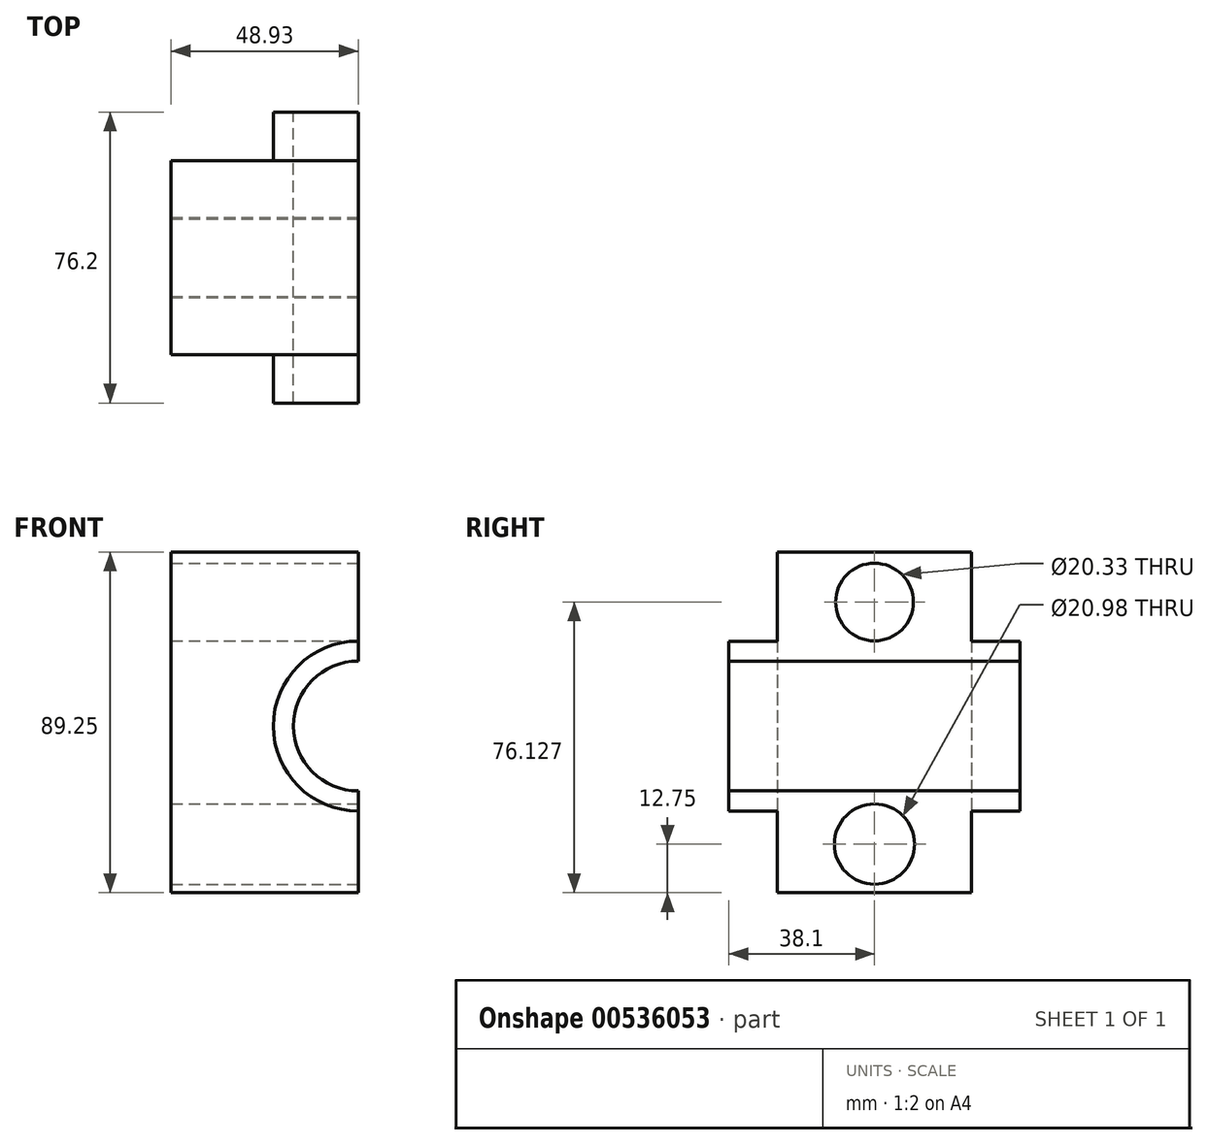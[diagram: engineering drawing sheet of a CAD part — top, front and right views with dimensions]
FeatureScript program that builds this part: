
annotation { "Feature Type Name" : "Feature", "Feature Type Description" : "" }
export const myFeature = defineFeature(function(context is Context, id is Id, definition is map)
    precondition{}
    {
        {
            var Q0;
            Q0=qCreatedBy(makeId("Front.planeOp"),FACE);
            var sketch = newSketch(context, id + "F0", { "sketchPlane" : qUnion([Q0])});
            skLineSegment(sketch, "E0.bottom", {"start": v(-48.93, 45.58) * mm, "end": v(47.02, 45.58) * mm});
            skLineSegment(sketch, "E0.top", {"start": v(-48.93, -43.67) * mm, "end": v(47.02, -43.67) * mm});
            skLineSegment(sketch, "E0.left", {"start": v(-48.93, 45.58) * mm, "end": v(-48.93, -43.67) * mm});
            skLineSegment(sketch, "E0.right", {"start": v(47.02, 45.58) * mm, "end": v(47.02, -43.67) * mm});
            skCircle(sketch, "E1", {"center": v(0, 0) * mm, "radius": 22.22 * mm});
            skCircle(sketch, "E2", {"center": v(0, 0) * mm, "radius": 16.98 * mm});
            skSolve(sketch);
        }
        {
            var Q0;
            Q0 = qSketchRegion(id + "F0", true);
            extrude(context, id + "F1", {"entities" : qUnion([Q0]), "endBound" : BoundingType.SYMMETRIC, "depth" : 50.8 * mm, "offsetDistance" : 25.4 * mm});
        }
        {
            var Q0;
            Q0=makeQuery(id+"F0.imprint","IMPRINT",FACE,{"disambiguationData":[TD([[makeQuery(id+"F0.imprint","IMPRINT",EDGE,{"derivedFrom":sQuery(id+"F0.wireOp",EDGE,"E1")}),1.0]])]});
            extrude(context, id + "F2", {"entities" : qUnion([Q0]), "operationType" : NewBodyOperationType.ADD, "endBound" : BoundingType.SYMMETRIC, "depth" : 76.2 * mm, "offsetDistance" : 25.4 * mm});
        }
        {
            var Q0;
            Q0=qCreatedBy(makeId("Top.planeOp"),FACE);
            var sketch = newSketch(context, id + "F3", { "sketchPlane" : qUnion([Q0])});
            skLineSegment(sketch, "E3", {"start": v(0, -54.5) * mm, "end": v(0, 50.05) * mm});
            skLineSegment(sketch, "E4", {"start": v(0, 50.05) * mm, "end": v(64.55, 41.44) * mm});
            skLineSegment(sketch, "E5", {"start": v(64.55, 41.44) * mm, "end": v(60.72, -51.32) * mm});
            skLineSegment(sketch, "E6", {"start": v(60.72, -51.32) * mm, "end": v(0, -54.5) * mm});
            skSolve(sketch);
        }
        {
            var Q0;
            Q0=makeQuery(id+"F3.imprint","IMPRINT",FACE,{"disambiguationData":[TD([[makeQuery(id+"F3.imprint","IMPRINT",EDGE,{"derivedFrom":sQuery(id+"F3.wireOp",EDGE,"E3")}),-1.0]])]});
            extrude(context, id + "F4", {"entities" : qUnion([Q0]), "operationType" : NewBodyOperationType.REMOVE, "endBound" : BoundingType.SYMMETRIC, "depth" : 1117.6 * mm, "offsetDistance" : 25.4 * mm});
        }
        {
            var Q0;
            Q0=qCreatedBy(makeId("Right.planeOp"),FACE);
            var sketch = newSketch(context, id + "F5", { "sketchPlane" : qUnion([Q0])});
            skCircle(sketch, "E7", {"center": v(0, -30.92) * mm, "radius": 10.5 * mm});
            skCircle(sketch, "E8", {"center": v(0, 32.46) * mm, "radius": 10.17 * mm});
            skSolve(sketch);
        }
        {
            var Q0;
            Q0=makeQuery(id+"F5.imprint","IMPRINT",FACE,{"disambiguationData":[TD([[makeQuery(id+"F5.imprint","IMPRINT",EDGE,{"derivedFrom":sQuery(id+"F5.wireOp",EDGE,"E7")}),1.0]])]});
            var Q1;
            Q1=makeQuery(id+"F5.imprint","IMPRINT",FACE,{"disambiguationData":[TD([[makeQuery(id+"F5.imprint","IMPRINT",EDGE,{"derivedFrom":sQuery(id+"F5.wireOp",EDGE,"E8")}),1.0]])]});
            extrude(context, id + "F6", {"entities" : qUnion([Q0, Q1]), "operationType" : NewBodyOperationType.REMOVE, "endBound" : BoundingType.THROUGH_ALL, "oppositeDirection" : true, "depth" : 25.4 * mm, "offsetDistance" : 25.4 * mm});
        }
    });
